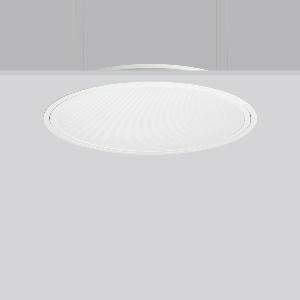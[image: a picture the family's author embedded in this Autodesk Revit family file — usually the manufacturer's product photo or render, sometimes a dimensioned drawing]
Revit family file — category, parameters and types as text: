
# Revit family: triona_round_e_312296_002_12_0944
name_source: partatom
category: Lighting Fixtures
units: mm (PartAtom-declared; Revit-internal decimal feet)

## family parameters
Cut with Voids When Loaded = No
Host = Face
Light Source = No
Part Type = Normal
Room Calculation Point = No
Round Connector Dimension = Use Diameter
Shared = No

## types (1)
- TRIONA round E (1 x LED Modul 830, 3750 lm, 3000)
    Apparent Load = 31 VA
    CIE Flux Codes = 58 86 97 100 100
    Color Rendering = 80
    Color Temperature = 3000
    Default Elevation = 1800 mm
    Description = Series: TRIONA round
Decorative round LED recessed surface luminaire. Cover made of sheet steel, powder-coated. Frame made of aluminium, powder-coated. Recessed ring: aluminium extrusion profile, powder coated. Light emission through a diffuser in plastic, opal/prismatic. Lightguide and diffuser made of non-yellowing plastic (PMMA). Lateral light emission (RZB SIDELITE technology) for above-average homogeneous light distribution. Suitable for installation in cavity ceilings. Tool-free mounting system thanks to the rocker arm mechanism (patent pending). Electronic ballast included. Very easy installation thanks to Plug+Play connection. Perfect for office areas (RUG < 19) and environments with computer screens in accordance with EN 12464-1. 
Colour: traffic white, matt (RAL 9016)
Diameter: 725 mm
Height: 2 mm
Cut-out diameter: 702 mm
Recess height: 100 mm
Luminaire: recess height: 89 mm
Lamp: LED
Socket: without socket
Colour temperature: 3000K
Colour rendering index (CRI): 80
System power: 31 W
Rated luminous flux: 3750 lm
Luminous efficiency: 121 lm/W
Control gear: Converter, dimmable, DALI
Protection class: I
Type of protection: IP 40
    Height = 0 mm  [stored 0 ft]
    Lamp = 1 x LED Modul 830
    Lamp Light Flux = 3750 lm
    Lamp count = 1
    Length = 725 mm
    Lifetime = 50000 h
    Luminous efficacy = 121 lm/W
    Manufacturer = RZB
    ModVariant = No
    Model = 312296.002.12
    Mounting Place = Ceiling
    Mounting Type = Recessed
    Number of Poles = 1
    OnlyDefault = Yes
    Power Factor = 1
    Product Name = TRIONA round E
    Product group = Recessed modular luminaires
    ProductGroupID = 406
    Protection Class = Protection class I
    Protection Degree = IP 20
    RLX_Detail_Level = 1
    RLX_Emergency_Light_Flux = 0 lm
    RLX_Emergency_Type = 0
    RLX_Emergency_Type_DB = No
    RlxData = <blob elided: 35617 chars, md5=7b499d75>
    Socket = socket
    Standby Power = 0 W
    System Light Flux = 3750 lm
    System Power = 31 W
    Type Comments = Product without accessories
    Type Image = 312296.002.12.jpg
    URL = http://relux.com
    VarID = ---
    Voltage = 230 V
    Voltage Range = 220-240 V
    Weight = 0.00 kg
    Width = 0 mm  [stored 0 ft]

note: [stored X ft] marks values corroborated as IEEE doubles in the binary element streams (Revit-internal decimal feet)

## geometry (parser evidence)
native form markers: Blend x4, Sweep x10
no freeform markers — native parametric forms only
